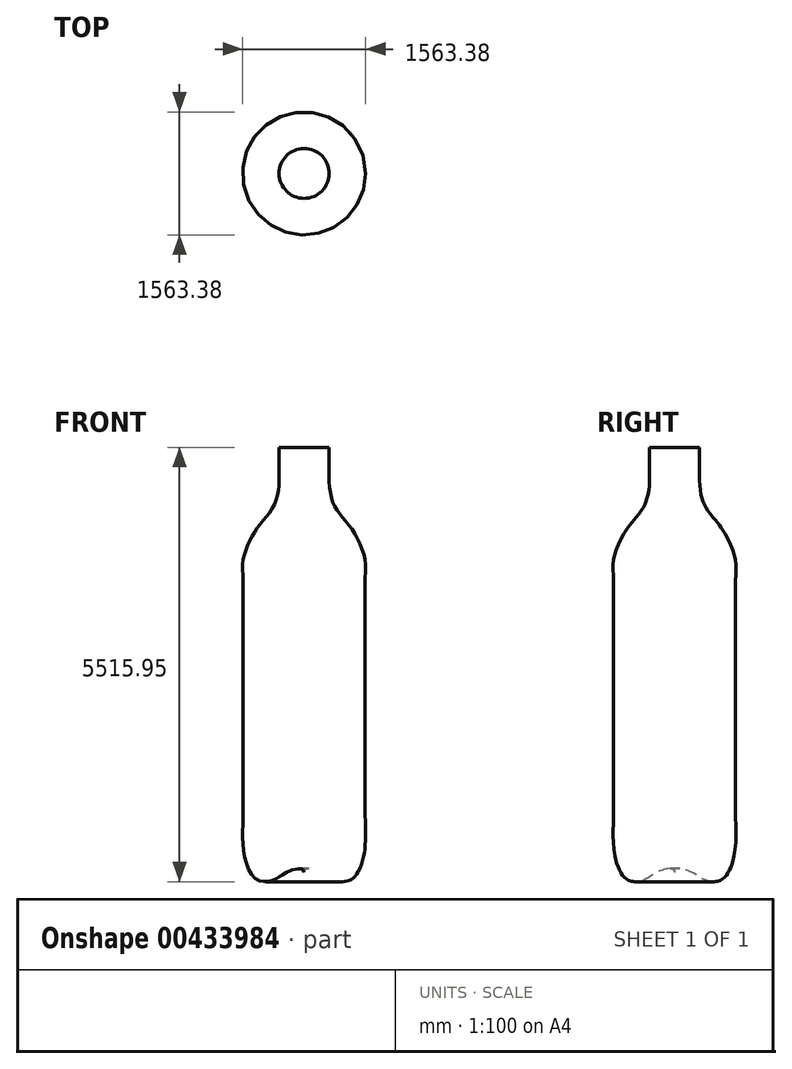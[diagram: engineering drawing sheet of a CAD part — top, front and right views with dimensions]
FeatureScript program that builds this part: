
annotation { "Feature Type Name" : "Feature", "Feature Type Description" : "" }
export const myFeature = defineFeature(function(context is Context, id is Id, definition is map)
    precondition{}
    {
        {
            var Q0;
            Q0=qCreatedBy(makeId("Front.planeOp"),FACE);
            var sketch = newSketch(context, id + "F0", { "sketchPlane" : qUnion([Q0])});
            skLineSegment(sketch, "E0", {"start": v(0, -232.4) * mm, "end": v(-317.5, -232.4) * mm});
            skLineSegment(sketch, "E1", {"start": v(0, -232.4) * mm, "end": v(0, -5629.9) * mm});
            skLineSegment(sketch, "E2", {"start": v(-317.5, -232.4) * mm, "end": v(-317.5, -588) * mm});
            skLineSegment(sketch, "E3", {"start": v(-774.7, -4867.74) * mm, "end": v(-774.7, -2935.31) * mm});
            skFitSpline(sketch, "E4", {"points": [v(0, -5629.9) * mm, v(-225.21, -5629.9) * mm, v(-388.96, -5728.79) * mm, v(-607.28, -5715.14) * mm, v(-771.03, -5333.07) * mm, v(-774.7, -4867.74) * mm], "startDerivative": vector(0, 1442.98) * mm, "endDerivative": vector(0, 1785.6) * mm});
            skLineSegment(sketch, "E5", {"start": v(-774.7, -2935.31) * mm, "end": v(-774.7, -1919.31) * mm});
            skFitSpline(sketch, "E6", {"points": [v(-774.7, -1919.31) * mm, v(-774.7, -1662.48) * mm, v(-593.64, -1253.11) * mm, v(-388.96, -980.2) * mm, v(-317.5, -588) * mm], "startDerivative": vector(0, 970.74) * mm, "endDerivative": vector(0, 1882.92) * mm});
            skSolve(sketch);
        }
        {
            var Q0;
            Q0=makeQuery(id+"F0.imprint","IMPRINT",FACE,{"disambiguationData":[TD([[makeQuery(id+"F0.imprint","IMPRINT",EDGE,{"derivedFrom":sQuery(id+"F0.wireOp",EDGE,"E0")}),1.0]])]});
            var Q1;
            Q1=sQuery(id+"F0.wireOp",EDGE,"E1");
            revolve(context, id + "F1", {"entities" : qUnion([Q0]), "axis" : qUnion([Q1]), "revolveType" : RevolveType.FULL});
        }
    });
